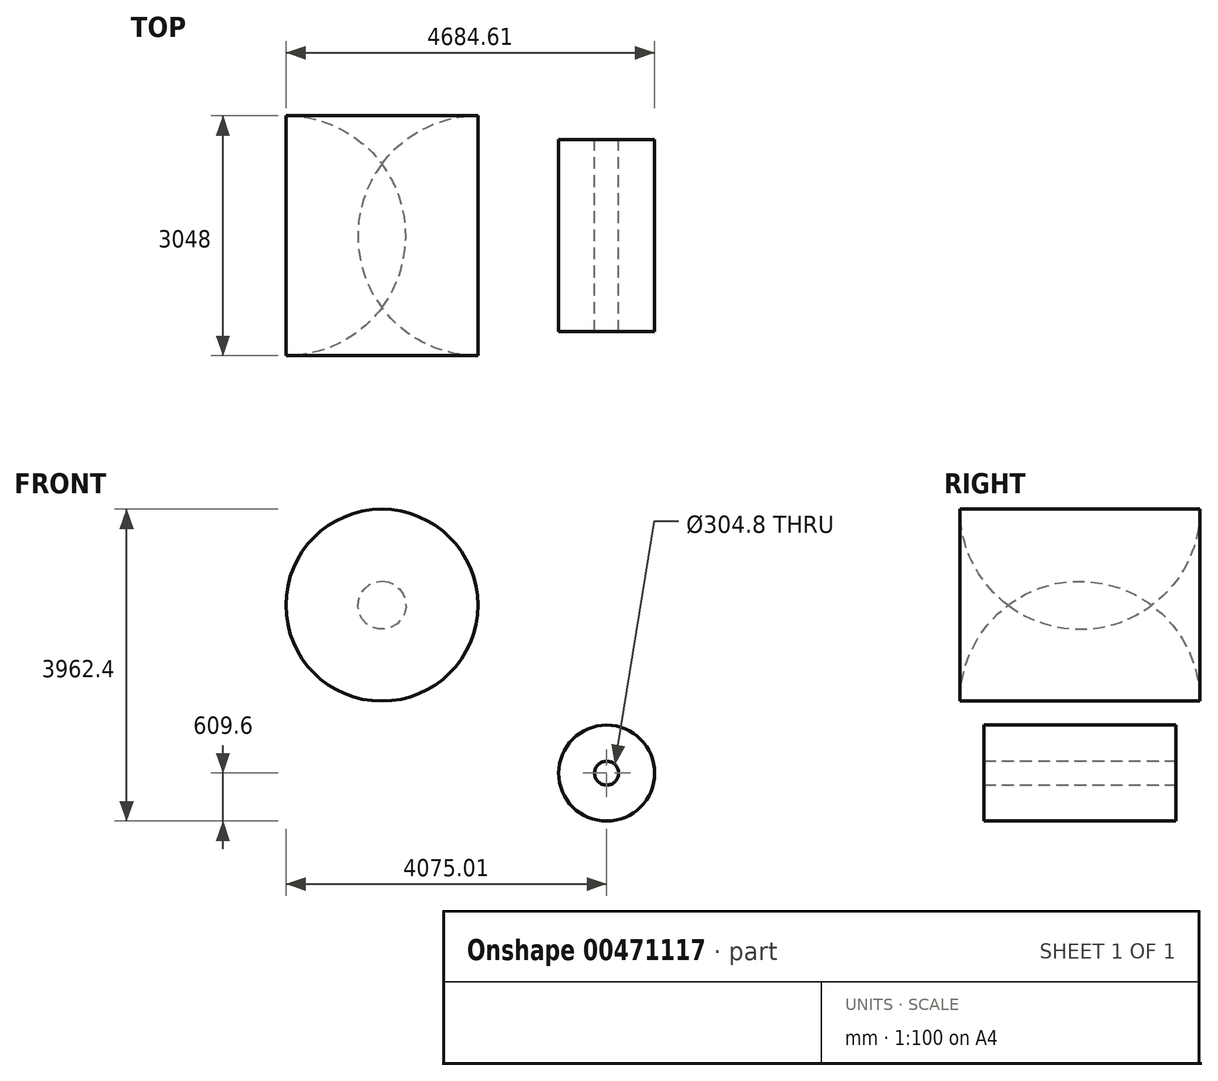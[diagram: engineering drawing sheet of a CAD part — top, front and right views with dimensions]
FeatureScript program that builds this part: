
annotation { "Feature Type Name" : "Feature", "Feature Type Description" : "" }
export const myFeature = defineFeature(function(context is Context, id is Id, definition is map)
    precondition{}
    {
        {
            var Q0;
            Q0=qCreatedBy(makeId("Front.planeOp"),FACE);
            var sketch = newSketch(context, id + "F0", { "sketchPlane" : qUnion([Q0])});
            skCircle(sketch, "E0", {"center": v(0, 2743.2) * mm, "radius": 2743.2 * mm});
            skCircle(sketch, "E1", {"center": v(0, 2743.2) * mm, "radius": 1219.2 * mm});
            skSolve(sketch);
        }
        {
            var Q0;
            Q0=makeQuery(id+"F0.imprint","IMPRINT",FACE,{"disambiguationData":[TD([[makeQuery(id+"F0.imprint","IMPRINT",EDGE,{"derivedFrom":sQuery(id+"F0.wireOp",EDGE,"E0")}),1.0]])]});
            extrude(context, id + "F1", {"entities" : qUnion([Q0]), "depth" : 3048 * mm});
        }
        {
            var Q0;
            Q0=makeQuery(id+"F1.opExtrude","CAP_EDGE",EDGE,{"disambiguationData":[OSD([sQuery(id+"F0.wireOp",EDGE,"E0")])],"isStart":false});
            var Q1;
            Q1=makeQuery(id+"F1.opExtrude","CAP_EDGE",EDGE,{"disambiguationData":[OSD([sQuery(id+"F0.wireOp",EDGE,"E0")])],"isStart":true});
            fillet(context, id + "F2", {"entities" : qUnion([Q0, Q1]), "radius" : 1524 * mm, "tangentPropagation" : true, "allowEdgeOverflow" : false});
        }
        {
            var Q0;
            Q0=qCreatedBy(makeId("Front.planeOp"),FACE);
            var sketch = newSketch(context, id + "F3", { "sketchPlane" : qUnion([Q0])});
            skLineSegment(sketch, "E2.bottom", {"start": v(3672.5, 304.8) * mm, "end": v(-1813.9, 304.8) * mm});
            skLineSegment(sketch, "E2.top", {"start": v(3672.5, 914.4) * mm, "end": v(-1813.9, 914.4) * mm});
            skLineSegment(sketch, "E2.left", {"start": v(3977.3, 609.6) * mm, "end": v(3977.3, 609.6) * mm});
            skLineSegment(sketch, "E2.right", {"start": v(-2118.7, 609.6) * mm, "end": v(-2118.7, 609.6) * mm});
            skPoint(sketch, "E3.visualSharp", {"position": v(3977.3, 914.4) * mm});
            skArc(sketch, "E3.filletArc", {"start": v(3977.3, 609.6) * mm, "mid": v(3888.02, 825.13) * mm, "end": v(3672.5, 914.4) * mm});
            skPoint(sketch, "E4.visualSharp", {"position": v(3977.3, 304.8) * mm});
            skArc(sketch, "E4.filletArc", {"start": v(3672.5, 304.8) * mm, "mid": v(3888.02, 394.07) * mm, "end": v(3977.3, 609.6) * mm});
            skPoint(sketch, "E5.visualSharp", {"position": v(-2118.7, 304.8) * mm});
            skArc(sketch, "E5.filletArc", {"start": v(-2118.7, 609.6) * mm, "mid": v(-2029.43, 394.07) * mm, "end": v(-1813.9, 304.8) * mm});
            skPoint(sketch, "E6.visualSharp", {"position": v(-2118.7, 914.4) * mm});
            skArc(sketch, "E6.filletArc", {"start": v(-1813.9, 914.4) * mm, "mid": v(-2029.43, 825.13) * mm, "end": v(-2118.7, 609.6) * mm});
            skSolve(sketch);
        }
        {
            var Q0;
            Q0 = qSketchRegion(id + "F3", true);
            extrude(context, id + "F4", {"entities" : qUnion([Q0]), "oppositeDirection" : true, "depth" : 152.4 * mm});
        }
        {
            var Q0;
            Q0=makeQuery(id+"F4.opExtrude","CAP_FACE",FACE,{"disambiguationData":[OSD([sQuery(id+"F3.wireOp",EDGE,"E2.bottom"),sQuery(id+"F3.wireOp",EDGE,"E2.top"),sQuery(id+"F3.wireOp",EDGE,"E2.left"),sQuery(id+"F3.wireOp",EDGE,"E2.right")])],"isStart":true});
            var sketch = newSketch(context, id + "F5", { "sketchPlane" : qUnion([Q0])});
            skCircle(sketch, "E7", {"center": v(2855.8, 609.6) * mm, "radius": 152.4 * mm});
            skSolve(sketch);
        }
        {
            var Q0;
            Q0 = qSketchRegion(id + "F5", true);
            extrude(context, id + "F6", {"entities" : qUnion([Q0]), "operationType" : NewBodyOperationType.ADD, "depth" : 304.8 * mm});
        }
        {
            var Q0;
            Q0=makeQuery(id+"F6.opExtrude","CAP_FACE",FACE,{"disambiguationData":[OSD([sQuery(id+"F5.wireOp",EDGE,"E7")])],"isStart":false});
            var sketch = newSketch(context, id + "F7", { "sketchPlane" : qUnion([Q0])});
            skCircle(sketch, "E8", {"center": v(2855.8, 609.6) * mm, "radius": 609.6 * mm});
            skSolve(sketch);
        }
        {
            var Q0;
            Q0=makeQuery(id+"F7.imprint","IMPRINT",FACE,{"disambiguationData":[TD([[makeQuery(id+"F7.imprint","IMPRINT",EDGE,{"derivedFrom":sQuery(id+"F7.wireOp",EDGE,"E8")}),1.0]])]});
            extrude(context, id + "F8", {"entities" : qUnion([Q0]), "depth" : 2438.4 * mm});
        }
        {
            var Q0;
            Q0=makeQuery(id+"F4.opExtrude","CAP_FACE",FACE,{"disambiguationData":[OSD([sQuery(id+"F3.wireOp",EDGE,"E2.bottom"),sQuery(id+"F3.wireOp",EDGE,"E2.top"),sQuery(id+"F3.wireOp",EDGE,"E2.left"),sQuery(id+"F3.wireOp",EDGE,"E2.right")])],"isStart":true});
            var sketch = newSketch(context, id + "F9", { "sketchPlane" : qUnion([Q0])});
            skCircle(sketch, "E9", {"center": v(-1813.9, 609.6) * mm, "radius": 304.8 * mm});
            skSolve(sketch);
        }
        {
            var Q0;
            {var subQ0=sQuery(id+"F9.wireOp",EDGE,"E9");var subQ1=makeQuery(id+"F9.imprint","INTERSECT",VERTEX,{"derivedFrom":[makeQuery(id+"F4.opExtrude","CAP_EDGE",EDGE,{"disambiguationData":[OSD([sQuery(id+"F3.wireOp",EDGE,"E2.right")])],"isStart":true}),subQ0]});Q0=makeQuery(id+"F9.imprint","IMPRINT",FACE,{"disambiguationData":[TD([[makeQuery(id+"F9.imprint","IMPRINT",EDGE,{"disambiguationData":[TD([[subQ1,1.0]])],"derivedFrom":subQ0}),1.0]])]});}
            extrude(context, id + "F10", {"entities" : qUnion([Q0]), "operationType" : NewBodyOperationType.ADD, "depth" : 3048 * mm});
        }
    });
